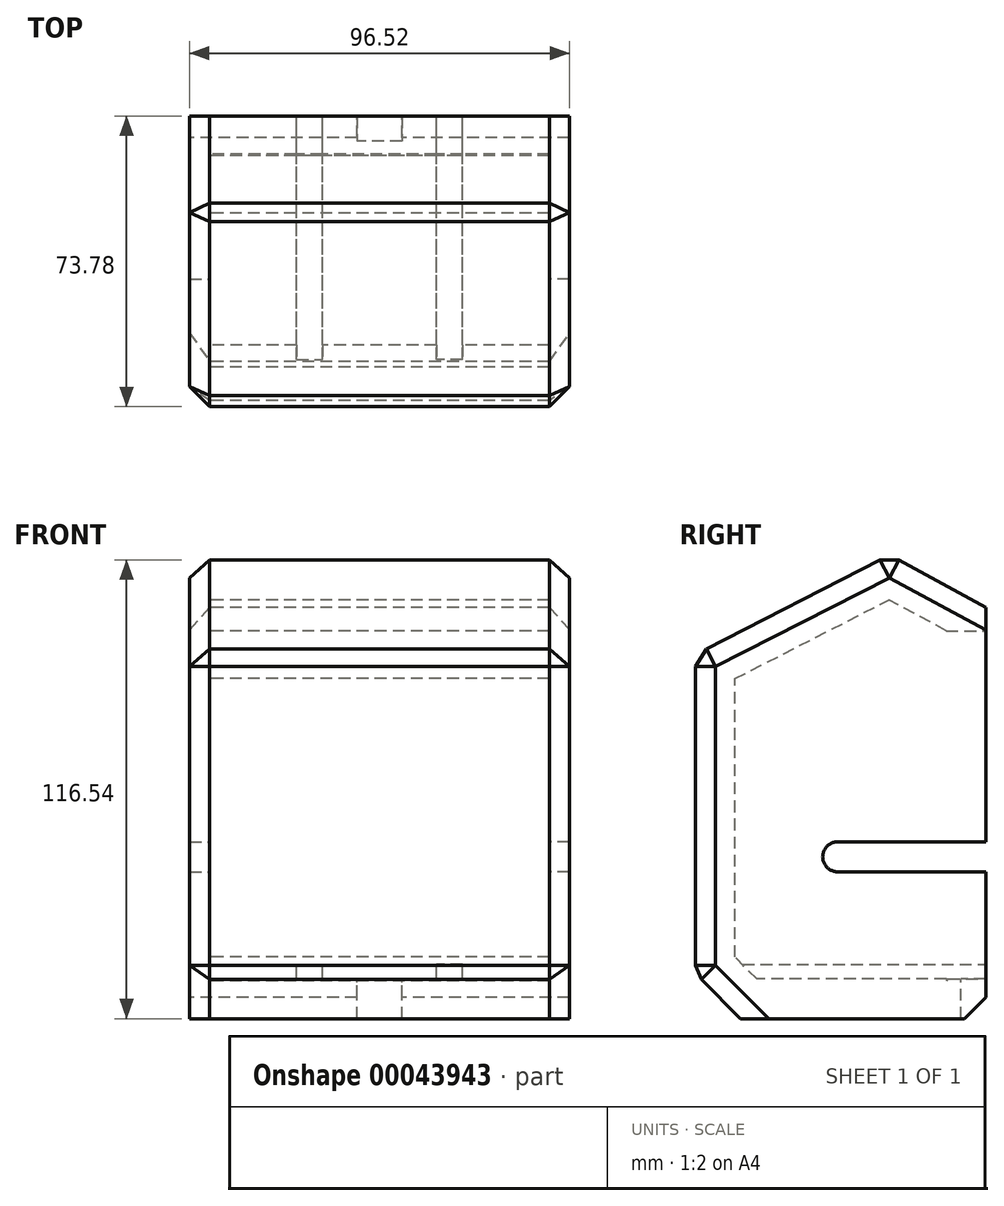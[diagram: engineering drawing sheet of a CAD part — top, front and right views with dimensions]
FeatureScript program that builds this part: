
annotation { "Feature Type Name" : "Feature", "Feature Type Description" : "" }
export const myFeature = defineFeature(function(context is Context, id is Id, definition is map)
    precondition{}
    {
        {
            var Q0;
            Q0=qCreatedBy(makeId("Right.planeOp"),FACE);
            var sketch = newSketch(context, id + "F0", { "sketchPlane" : qUnion([Q0])});
            skLineSegment(sketch, "E0", {"start": v(-39.9, 44.8) * mm, "end": v(9.41, 70.01) * mm});
            skLineSegment(sketch, "E1", {"start": v(33.89, 56.8) * mm, "end": v(9.41, 70.01) * mm});
            skLineSegment(sketch, "E2", {"start": v(33.89, 56.8) * mm, "end": v(33.89, -42.27) * mm});
            skLineSegment(sketch, "E3", {"start": v(33.89, -42.27) * mm, "end": v(28.42, -47.74) * mm});
            skLineSegment(sketch, "E4", {"start": v(28.42, -47.74) * mm, "end": v(-28.42, -47.74) * mm});
            skLineSegment(sketch, "E5", {"start": v(-28.42, -47.74) * mm, "end": v(-39.9, -36.27) * mm});
            skLineSegment(sketch, "E6", {"start": v(-39.9, -36.27) * mm, "end": v(-39.9, 44.8) * mm});
            skLineSegment(sketch, "E7.0", {"start": v(24.25, -37.68) * mm, "end": v(-24.25, -37.68) * mm});
            skLineSegment(sketch, "E7.1", {"start": v(24.25, -37.68) * mm, "end": v(23.83, -38.1) * mm});
            skLineSegment(sketch, "E7.2", {"start": v(-29.83, -32.1) * mm, "end": v(-29.83, 38.66) * mm});
            skLineSegment(sketch, "E7.3", {"start": v(-29.83, 38.66) * mm, "end": v(9.28, 58.65) * mm});
            skLineSegment(sketch, "E7.4", {"start": v(23.83, 50.8) * mm, "end": v(9.28, 58.65) * mm});
            skLineSegment(sketch, "E7.5", {"start": v(-24.25, -37.68) * mm, "end": v(-29.83, -32.1) * mm});
            skLineSegment(sketch, "E7.6", {"start": v(23.83, 50.8) * mm, "end": v(23.83, -38.1) * mm});
            skLineSegment(sketch, "E8", {"start": v(23.83, 50.8) * mm, "end": v(33.89, 50.8) * mm});
            skLineSegment(sketch, "E9", {"start": v(24.25, -37.68) * mm, "end": v(33.89, -37.68) * mm});
            skSolve(sketch);
        }
        {
            var Q0;
            Q0=makeQuery(id+"F0.imprint","IMPRINT",FACE,{"disambiguationData":[TD([[makeQuery(id+"F0.imprint","IMPRINT",EDGE,{"derivedFrom":sQuery(id+"F0.wireOp",EDGE,"E0")}),-1.0]])]});
            extrude(context, id + "F1", {"entities" : qUnion([Q0]), "endBound" : BoundingType.SYMMETRIC, "depth" : 86.36 * mm});
        }
        {
            var Q0;
            Q0=makeQuery(id+"F1.opExtrude","CAP_FACE",FACE,{"disambiguationData":[OSD([sQuery(id+"F0.wireOp",EDGE,"E0"),sQuery(id+"F0.wireOp",EDGE,"E1"),sQuery(id+"F0.wireOp",EDGE,"E2"),sQuery(id+"F0.wireOp",EDGE,"E3"),sQuery(id+"F0.wireOp",EDGE,"E4"),sQuery(id+"F0.wireOp",EDGE,"E5"),sQuery(id+"F0.wireOp",EDGE,"E6"),sQuery(id+"F0.wireOp",EDGE,"E7.0"),sQuery(id+"F0.wireOp",EDGE,"E7.1"),sQuery(id+"F0.wireOp",EDGE,"E7.2"),sQuery(id+"F0.wireOp",EDGE,"E7.3"),sQuery(id+"F0.wireOp",EDGE,"E7.4"),sQuery(id+"F0.wireOp",EDGE,"E7.5"),sQuery(id+"F0.wireOp",EDGE,"E7.6"),sQuery(id+"F0.wireOp",EDGE,"E8"),sQuery(id+"F0.wireOp",EDGE,"E9")])],"isStart":false});
            var sketch = newSketch(context, id + "F2", { "sketchPlane" : qUnion([Q0])});
            skLineSegment(sketch, "E10.0.0", {"start": v(9.41, 70.01) * mm, "end": v(-39.9, 44.8) * mm});
            skLineSegment(sketch, "E10.0.1", {"start": v(-39.9, 44.8) * mm, "end": v(-39.9, -36.27) * mm});
            skLineSegment(sketch, "E10.0.2", {"start": v(-39.9, -36.27) * mm, "end": v(-28.42, -47.74) * mm});
            skLineSegment(sketch, "E10.0.3", {"start": v(-28.42, -47.74) * mm, "end": v(28.42, -47.74) * mm});
            skLineSegment(sketch, "E10.0.4", {"start": v(28.42, -47.74) * mm, "end": v(33.89, -42.27) * mm});
            skLineSegment(sketch, "E10.0.5", {"start": v(33.89, -42.27) * mm, "end": v(33.89, -37.68) * mm});
            skLineSegment(sketch, "E10.0.6", {"start": v(33.89, -37.68) * mm, "end": v(24.25, -37.68) * mm});
            skLineSegment(sketch, "E10.0.7", {"start": v(24.25, -37.68) * mm, "end": v(23.83, -38.1) * mm});
            skLineSegment(sketch, "E10.0.8", {"start": v(23.83, -38.1) * mm, "end": v(23.83, -37.68) * mm});
            skLineSegment(sketch, "E10.0.9", {"start": v(23.83, -37.68) * mm, "end": v(-24.25, -37.68) * mm});
            skLineSegment(sketch, "E10.0.10", {"start": v(-24.25, -37.68) * mm, "end": v(-29.83, -32.1) * mm});
            skLineSegment(sketch, "E10.0.11", {"start": v(-29.83, -32.1) * mm, "end": v(-29.83, 38.66) * mm});
            skLineSegment(sketch, "E10.0.12", {"start": v(-29.83, 38.66) * mm, "end": v(9.28, 58.65) * mm});
            skLineSegment(sketch, "E10.0.13", {"start": v(9.28, 58.65) * mm, "end": v(23.83, 50.8) * mm});
            skLineSegment(sketch, "E10.0.14", {"start": v(23.83, 50.8) * mm, "end": v(33.89, 50.8) * mm});
            skLineSegment(sketch, "E10.0.15", {"start": v(33.89, 50.8) * mm, "end": v(33.89, 56.8) * mm});
            skLineSegment(sketch, "E10.0.16", {"start": v(33.89, 56.8) * mm, "end": v(9.41, 70.01) * mm});
            skLineSegment(sketch, "E11", {"start": v(24.25, -37.68) * mm, "end": v(23.83, 50.8) * mm});
            skLineSegment(sketch, "E12", {"start": v(33.89, 50.8) * mm, "end": v(33.89, -37.68) * mm});
            skSolve(sketch);
        }
        {
            var Q0;
            Q0 = qSketchRegion(id + "F2", true);
            var Q1;
            Q1=makeQuery(id+"F2.imprint","IMPRINT",FACE,{"disambiguationData":[TD([[makeQuery(id+"F2.imprint","IMPRINT",EDGE,{"derivedFrom":sQuery(id+"F2.wireOp",EDGE,"E10.0.7")}),-1.0]])]});
            extrude(context, id + "F3", {"entities" : qUnion([Q0, Q1]), "operationType" : NewBodyOperationType.ADD, "depth" : 5.08 * mm});
        }
        {
            var Q0;
            Q0=makeQuery(id+"F1.opExtrude","CAP_FACE",FACE,{"disambiguationData":[OSD([sQuery(id+"F0.wireOp",EDGE,"E0"),sQuery(id+"F0.wireOp",EDGE,"E1"),sQuery(id+"F0.wireOp",EDGE,"E2"),sQuery(id+"F0.wireOp",EDGE,"E3"),sQuery(id+"F0.wireOp",EDGE,"E4"),sQuery(id+"F0.wireOp",EDGE,"E5"),sQuery(id+"F0.wireOp",EDGE,"E6"),sQuery(id+"F0.wireOp",EDGE,"E7.0"),sQuery(id+"F0.wireOp",EDGE,"E7.1"),sQuery(id+"F0.wireOp",EDGE,"E7.2"),sQuery(id+"F0.wireOp",EDGE,"E7.3"),sQuery(id+"F0.wireOp",EDGE,"E7.4"),sQuery(id+"F0.wireOp",EDGE,"E7.5"),sQuery(id+"F0.wireOp",EDGE,"E7.6"),sQuery(id+"F0.wireOp",EDGE,"E8"),sQuery(id+"F0.wireOp",EDGE,"E9")])],"isStart":true});
            var sketch = newSketch(context, id + "F4", { "sketchPlane" : qUnion([Q0])});
            skLineSegment(sketch, "E13.0.0", {"start": v(39.9, 44.8) * mm, "end": v(-9.41, 70.01) * mm});
            skLineSegment(sketch, "E13.0.1", {"start": v(-9.41, 70.01) * mm, "end": v(-33.89, 56.8) * mm});
            skLineSegment(sketch, "E13.0.2", {"start": v(-33.89, 56.8) * mm, "end": v(-33.89, 50.8) * mm});
            skLineSegment(sketch, "E13.0.3", {"start": v(-33.89, 50.8) * mm, "end": v(-23.83, 50.8) * mm});
            skLineSegment(sketch, "E13.0.4", {"start": v(-23.83, 50.8) * mm, "end": v(-9.28, 58.65) * mm});
            skLineSegment(sketch, "E13.0.5", {"start": v(-9.28, 58.65) * mm, "end": v(29.83, 38.66) * mm});
            skLineSegment(sketch, "E13.0.6", {"start": v(29.83, 38.66) * mm, "end": v(29.83, -32.1) * mm});
            skLineSegment(sketch, "E13.0.7", {"start": v(29.83, -32.1) * mm, "end": v(24.25, -37.68) * mm});
            skLineSegment(sketch, "E13.0.8", {"start": v(24.25, -37.68) * mm, "end": v(-23.83, -37.68) * mm});
            skLineSegment(sketch, "E13.0.9", {"start": v(-23.83, -37.68) * mm, "end": v(-23.83, -38.1) * mm});
            skLineSegment(sketch, "E13.0.10", {"start": v(-23.83, -38.1) * mm, "end": v(-24.25, -37.68) * mm});
            skLineSegment(sketch, "E13.0.11", {"start": v(-24.25, -37.68) * mm, "end": v(-33.89, -37.68) * mm});
            skLineSegment(sketch, "E13.0.12", {"start": v(-33.89, -37.68) * mm, "end": v(-33.89, -42.27) * mm});
            skLineSegment(sketch, "E13.0.13", {"start": v(-33.89, -42.27) * mm, "end": v(-28.42, -47.74) * mm});
            skLineSegment(sketch, "E13.0.14", {"start": v(-28.42, -47.74) * mm, "end": v(28.42, -47.74) * mm});
            skLineSegment(sketch, "E13.0.15", {"start": v(28.42, -47.74) * mm, "end": v(39.9, -36.27) * mm});
            skLineSegment(sketch, "E13.0.16", {"start": v(39.9, -36.27) * mm, "end": v(39.9, 44.8) * mm});
            skLineSegment(sketch, "E14", {"start": v(-33.89, 50.8) * mm, "end": v(-33.89, -37.68) * mm});
            skLineSegment(sketch, "E15", {"start": v(-23.83, -37.68) * mm, "end": v(-23.83, 50.8) * mm});
            skSolve(sketch);
        }
        {
            var Q0;
            Q0 = qSketchRegion(id + "F4", true);
            var Q1;
            Q1=makeQuery(id+"F4.imprint","IMPRINT",FACE,{"disambiguationData":[TD([[makeQuery(id+"F4.imprint","IMPRINT",EDGE,{"derivedFrom":sQuery(id+"F4.wireOp",EDGE,"E13.0.4")}),-1.0]])]});
            extrude(context, id + "F5", {"entities" : qUnion([Q0, Q1]), "operationType" : NewBodyOperationType.ADD, "depth" : 5.08 * mm});
        }
        {
            var Q0;
            {var subQ0=sQuery(id+"F0.wireOp",EDGE,"E2");Q0=makeQuery(id+"F5.boolean.opBoolean","MERGE",FACE,{"derivedFrom":[makeQuery(id+"F3.boolean.opBoolean","MERGE",FACE,{"derivedFrom":[makeQuery(id+"F1.opExtrude","SWEPT_FACE",FACE,{"disambiguationData":[OSD([subQ0]),TDD([makeQuery(id+"F0.imprint","IMPRINT",EDGE,{"disambiguationData":[TD([[makeQuery(id+"F0.imprint","INTERSECT",VERTEX,{"derivedFrom":[sQuery(id+"F0.wireOp",EDGE,"E1"),subQ0]}),-1.0]])],"derivedFrom":subQ0})])]}),makeQuery(id+"F1.opExtrude","SWEPT_FACE",FACE,{"disambiguationData":[OSD([subQ0]),TDD([makeQuery(id+"F0.imprint","IMPRINT",EDGE,{"disambiguationData":[TD([[makeQuery(id+"F0.imprint","INTERSECT",VERTEX,{"derivedFrom":[subQ0,sQuery(id+"F0.wireOp",EDGE,"E3")]}),1.0]])],"derivedFrom":subQ0})])]}),makeQuery(id+"F3.opExtrude","SWEPT_FACE",FACE,{"disambiguationData":[OSD([sQuery(id+"F2.wireOp",EDGE,"E10.0.5"),sQuery(id+"F2.wireOp",EDGE,"E10.0.15"),sQuery(id+"F2.wireOp",EDGE,"E12")])]})]}),makeQuery(id+"F5.opExtrude","SWEPT_FACE",FACE,{"disambiguationData":[OSD([sQuery(id+"F4.wireOp",EDGE,"E13.0.2"),sQuery(id+"F4.wireOp",EDGE,"E13.0.12"),sQuery(id+"F4.wireOp",EDGE,"E14")])]})]});}
            var sketch = newSketch(context, id + "F6", { "sketchPlane" : qUnion([Q0])});
            skLineSegment(sketch, "E16", {"start": v(4.02, 50.8) * mm, "end": v(4.02, -37.68) * mm, "construction": true});
            skSolve(sketch);
        }
        {
            var Q0;
            {var subQ0=sQuery(id+"F0.wireOp",EDGE,"E2");Q0=makeQuery(id+"F6.imprint","IMPRINT",FACE,{"disambiguationData":[TD([[makeQuery(id+"F6.imprint","IMPRINT",EDGE,{"derivedFrom":makeQuery(id+"F1.opExtrude","SWEPT_EDGE",EDGE,{"disambiguationData":[OSD([subQ0,sQuery(id+"F0.wireOp",EDGE,"E8")])]})}),-1.0]])]});}
            var sketch = newSketch(context, id + "F7", { "sketchPlane" : qUnion([Q0])});
            skLineSegment(sketch, "E17.0", {"start": v(-43.18, -37.68) * mm, "end": v(43.18, -37.68) * mm});
            skLineSegment(sketch, "E18.bottom", {"start": v(-21.08, -37.68) * mm, "end": v(-14.48, -37.68) * mm});
            skLineSegment(sketch, "E18.top", {"start": v(-21.08, -34) * mm, "end": v(-14.48, -34) * mm});
            skLineSegment(sketch, "E18.left", {"start": v(-21.08, -37.68) * mm, "end": v(-21.08, -34) * mm});
            skLineSegment(sketch, "E18.right", {"start": v(-14.48, -37.68) * mm, "end": v(-14.48, -34) * mm});
            skLineSegment(sketch, "E19.MirrorCS", {"start": v(21.08, -34) * mm, "end": v(14.48, -34) * mm});
            skLineSegment(sketch, "E20.MirrorCS", {"start": v(14.48, -37.68) * mm, "end": v(14.48, -34) * mm});
            skLineSegment(sketch, "E21.MirrorCS", {"start": v(21.08, -37.68) * mm, "end": v(21.08, -34) * mm});
            skLineSegment(sketch, "E22.MirrorCS", {"start": v(21.08, -37.68) * mm, "end": v(14.48, -37.68) * mm});
            skLineSegment(sketch, "E23", {"start": v(-17.78, -34) * mm, "end": v(17.78, -34) * mm, "construction": true});
            skSolve(sketch);
        }
        {
            var Q0;
            Q0 = qSketchRegion(id + "F7", true);
            var Q1;
            Q1=makeQuery(id+"F1.opExtrude","SWEPT_FACE",FACE,{"disambiguationData":[OSD([sQuery(id+"F0.wireOp",EDGE,"E7.5")])]});
            extrude(context, id + "F8", {"entities" : qUnion([Q0]), "operationType" : NewBodyOperationType.ADD, "endBound" : BoundingType.UP_TO_SURFACE, "oppositeDirection" : true, "endBoundEntityFace" : qUnion([Q1]), "depth" : 25.4 * mm});
        }
        {
            var Q0;
            {var subQ1=sQuery(id+"F7.wireOp",EDGE,"E18.right");var subQ5=sQuery(id+"F0.wireOp",EDGE,"E9");Q0=makeQuery(id+"F8.boolean.opBoolean","SPLIT",FACE,{"disambiguationData":[TD([makeQuery(id+"F8.opExtrude","SWEPT_FACE",FACE,{"disambiguationData":[OSD([subQ1])]})])],"derivedFrom":makeQuery(id+"F1.opExtrude","SWEPT_FACE",FACE,{"disambiguationData":[OSD([subQ5])]})});}
            var sketch = newSketch(context, id + "F9", { "sketchPlane" : qUnion([Q0])});
            skLineSegment(sketch, "E24.bottom", {"start": v(5.72, 33.89) * mm, "end": v(-5.71, 33.89) * mm});
            skLineSegment(sketch, "E24.top", {"start": v(5.72, 27.54) * mm, "end": v(-5.71, 27.54) * mm});
            skLineSegment(sketch, "E24.left", {"start": v(5.72, 33.89) * mm, "end": v(5.72, 27.54) * mm});
            skLineSegment(sketch, "E24.right", {"start": v(-5.71, 33.89) * mm, "end": v(-5.71, 27.54) * mm});
            skLineSegment(sketch, "E25", {"start": v(0, 27.54) * mm, "end": v(0, 33.89) * mm, "construction": true});
            skSolve(sketch);
        }
        {
            var Q0;
            Q0 = qSketchRegion(id + "F9", true);
            var Q1;
            Q1=makeQuery(id+"F5.boolean.opBoolean","MERGE",FACE,{"derivedFrom":[makeQuery(id+"F3.boolean.opBoolean","MERGE",FACE,{"derivedFrom":[makeQuery(id+"F1.opExtrude","SWEPT_FACE",FACE,{"disambiguationData":[OSD([sQuery(id+"F0.wireOp",EDGE,"E4")])]}),makeQuery(id+"F3.opExtrude","SWEPT_FACE",FACE,{"disambiguationData":[OSD([sQuery(id+"F2.wireOp",EDGE,"E10.0.3")])]})]}),makeQuery(id+"F5.opExtrude","SWEPT_FACE",FACE,{"disambiguationData":[OSD([sQuery(id+"F4.wireOp",EDGE,"E13.0.14")])]})]});
            extrude(context, id + "F10", {"entities" : qUnion([Q0]), "operationType" : NewBodyOperationType.REMOVE, "endBound" : BoundingType.UP_TO_SURFACE, "oppositeDirection" : true, "endBoundEntityFace" : qUnion([Q1]), "depth" : 25.4 * mm});
        }
        {
            var Q0;
            Q0=makeQuery(id+"F3.opExtrude","CAP_FACE",FACE,{"disambiguationData":[OSD([sQuery(id+"F2.wireOp",EDGE,"E10.0.0"),sQuery(id+"F2.wireOp",EDGE,"E10.0.1"),sQuery(id+"F2.wireOp",EDGE,"E10.0.2"),sQuery(id+"F2.wireOp",EDGE,"E10.0.3"),sQuery(id+"F2.wireOp",EDGE,"E10.0.4"),sQuery(id+"F2.wireOp",EDGE,"E10.0.5"),sQuery(id+"F2.wireOp",EDGE,"E10.0.15"),sQuery(id+"F2.wireOp",EDGE,"E10.0.16"),sQuery(id+"F2.wireOp",EDGE,"E12")])],"isStart":true});
            var sketch = newSketch(context, id + "F11", { "sketchPlane" : qUnion([Q0])});
            skLineSegment(sketch, "E26", {"start": v(3.75, -37.68) * mm, "end": v(3.75, -6.62) * mm, "construction": true});
            skCircle(sketch, "E27", {"center": v(3.75, -6.62) * mm, "radius": 3.81 * mm});
            skPoint(sketch, "E28.endSnap0", {"position": v(-33.89, 6.56) * mm});
            skLineSegment(sketch, "E29", {"start": v(3.73, -2.8) * mm, "end": v(-33.89, -2.8) * mm});
            skLineSegment(sketch, "E30", {"start": v(3.75, -10.43) * mm, "end": v(-33.89, -10.43) * mm});
            skSolve(sketch);
        }
        {
            var Q0;
            Q0 = qSketchRegion(id + "F11", true);
            var Q1;
            {var subQ2=sQuery(id+"F11.wireOp",EDGE,"aea72d7a-da8c-434c-a6ff-f5a4e8493872");Q1=makeQuery(id+"F11.imprint","IMPRINT",FACE,{"disambiguationData":[TD([[makeQuery(id+"F11.imprint","IMPRINT",EDGE,{"derivedFrom":subQ2}),-1.0]])]});}
            var Q2;
            {var subQ2=sQuery(id+"F11.wireOp",EDGE,"E29");Q2=makeQuery(id+"F11.imprint","IMPRINT",FACE,{"disambiguationData":[TD([[makeQuery(id+"F11.imprint","IMPRINT",EDGE,{"derivedFrom":subQ2}),1.0]])]});}
            extrude(context, id + "F12", {"entities" : qUnion([Q0, Q1, Q2]), "operationType" : NewBodyOperationType.REMOVE, "endBound" : BoundingType.THROUGH_ALL, "depth" : 25.4 * mm});
        }
        {
            var Q0;
            Q0 = qSketchRegion(id + "F11", true);
            var Q1;
            {var subQ2=sQuery(id+"F11.wireOp",EDGE,"aea72d7a-da8c-434c-a6ff-f5a4e8493872");Q1=makeQuery(id+"F11.imprint","IMPRINT",FACE,{"disambiguationData":[TD([[makeQuery(id+"F11.imprint","IMPRINT",EDGE,{"derivedFrom":subQ2}),-1.0]])]});}
            var Q2;
            {var subQ2=sQuery(id+"F11.wireOp",EDGE,"E29");Q2=makeQuery(id+"F11.imprint","IMPRINT",FACE,{"disambiguationData":[TD([[makeQuery(id+"F11.imprint","IMPRINT",EDGE,{"derivedFrom":subQ2}),1.0]])]});}
            extrude(context, id + "F13", {"entities" : qUnion([Q0, Q1, Q2]), "operationType" : NewBodyOperationType.REMOVE, "endBound" : BoundingType.THROUGH_ALL, "oppositeDirection" : true, "depth" : 25.4 * mm});
        }
        {
            var Q0;
            Q0=makeQuery(id+"F3.opExtrude","CAP_EDGE",EDGE,{"disambiguationData":[OSD([sQuery(id+"F2.wireOp",EDGE,"E10.0.1")])],"isStart":false});
            var Q1;
            Q1=makeQuery(id+"F5.opExtrude","CAP_EDGE",EDGE,{"disambiguationData":[OSD([sQuery(id+"F4.wireOp",EDGE,"E13.0.16")])],"isStart":false});
            var Q2;
            Q2=makeQuery(id+"F5.opExtrude","CAP_EDGE",EDGE,{"disambiguationData":[OSD([sQuery(id+"F4.wireOp",EDGE,"E13.0.15")])],"isStart":false});
            var Q3;
            Q3=makeQuery(id+"F3.opExtrude","CAP_EDGE",EDGE,{"disambiguationData":[OSD([sQuery(id+"F2.wireOp",EDGE,"E10.0.2")])],"isStart":false});
            var Q4;
            Q4=makeQuery(id+"F5.opExtrude","CAP_EDGE",EDGE,{"disambiguationData":[OSD([sQuery(id+"F4.wireOp",EDGE,"E13.0.0")])],"isStart":false});
            var Q5;
            Q5=makeQuery(id+"F3.opExtrude","CAP_EDGE",EDGE,{"disambiguationData":[OSD([sQuery(id+"F2.wireOp",EDGE,"E10.0.0")])],"isStart":false});
            var Q6;
            Q6=makeQuery(id+"F5.opExtrude","CAP_EDGE",EDGE,{"disambiguationData":[OSD([sQuery(id+"F4.wireOp",EDGE,"E13.0.1")])],"isStart":false});
            var Q7;
            Q7=makeQuery(id+"F3.opExtrude","CAP_EDGE",EDGE,{"disambiguationData":[OSD([sQuery(id+"F2.wireOp",EDGE,"E10.0.16")])],"isStart":false});
            var Q8;
            Q8=makeQuery(id+"F5.boolean.opBoolean","MERGE",EDGE,{"derivedFrom":[makeQuery(id+"F3.boolean.opBoolean","MERGE",EDGE,{"derivedFrom":[makeQuery(id+"F1.opExtrude","SWEPT_EDGE",EDGE,{"disambiguationData":[OSD([sQuery(id+"F0.wireOp",EDGE,"E0"),sQuery(id+"F0.wireOp",EDGE,"E1")])]}),makeQuery(id+"F3.opExtrude","SWEPT_EDGE",EDGE,{"disambiguationData":[OSD([sQuery(id+"F2.wireOp",EDGE,"E10.0.0"),sQuery(id+"F2.wireOp",EDGE,"E10.0.16")])]})]}),makeQuery(id+"F5.opExtrude","SWEPT_EDGE",EDGE,{"disambiguationData":[OSD([sQuery(id+"F4.wireOp",EDGE,"E13.0.0"),sQuery(id+"F4.wireOp",EDGE,"E13.0.1")])]})]});
            var Q9;
            Q9=makeQuery(id+"F5.boolean.opBoolean","MERGE",EDGE,{"derivedFrom":[makeQuery(id+"F3.boolean.opBoolean","MERGE",EDGE,{"derivedFrom":[makeQuery(id+"F1.opExtrude","SWEPT_EDGE",EDGE,{"disambiguationData":[OSD([sQuery(id+"F0.wireOp",EDGE,"E0"),sQuery(id+"F0.wireOp",EDGE,"E6")])]}),makeQuery(id+"F3.opExtrude","SWEPT_EDGE",EDGE,{"disambiguationData":[OSD([sQuery(id+"F2.wireOp",EDGE,"E10.0.0"),sQuery(id+"F2.wireOp",EDGE,"E10.0.1")])]})]}),makeQuery(id+"F5.opExtrude","SWEPT_EDGE",EDGE,{"disambiguationData":[OSD([sQuery(id+"F4.wireOp",EDGE,"E13.0.0"),sQuery(id+"F4.wireOp",EDGE,"E13.0.16")])]})]});
            var Q10;
            Q10=makeQuery(id+"F5.boolean.opBoolean","MERGE",EDGE,{"derivedFrom":[makeQuery(id+"F3.boolean.opBoolean","MERGE",EDGE,{"derivedFrom":[makeQuery(id+"F1.opExtrude","SWEPT_EDGE",EDGE,{"disambiguationData":[OSD([sQuery(id+"F0.wireOp",EDGE,"E5"),sQuery(id+"F0.wireOp",EDGE,"E6")])]}),makeQuery(id+"F3.opExtrude","SWEPT_EDGE",EDGE,{"disambiguationData":[OSD([sQuery(id+"F2.wireOp",EDGE,"E10.0.1"),sQuery(id+"F2.wireOp",EDGE,"E10.0.2")])]})]}),makeQuery(id+"F5.opExtrude","SWEPT_EDGE",EDGE,{"disambiguationData":[OSD([sQuery(id+"F4.wireOp",EDGE,"E13.0.15"),sQuery(id+"F4.wireOp",EDGE,"E13.0.16")])]})]});
            chamfer(context, id + "F14", {"entities" : qUnion([Q0, Q1, Q2, Q3, Q4, Q5, Q6, Q7, Q8, Q9, Q10]), "width" : 5.08 * mm, "tangentPropagation" : true});
        }
    });
